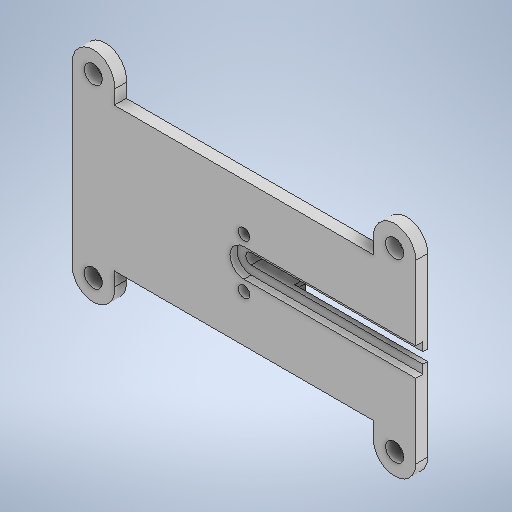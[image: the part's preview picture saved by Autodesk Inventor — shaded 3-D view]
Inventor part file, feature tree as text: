
AUTODESK INVENTOR PART (.ipt)
format: ipt  version: 2025.1 (Build 291241000, 241)  size: 326,656 bytes
history: native  units: mm
features: extrude x4, sketch x4
ambient origin geometry x8: Origin, YZ Plane, XZ Plane, XY Plane, X Axis, Y Axis, Z Axis, Center Point
bodies: Solid1 (feature_tree)
feature tree (8):
  extrude  "Extrusion1"  Depth=15.5mm
  extrude  "Extrusion2"  Depth=2.48mm
  extrude  "Extrusion3"  Depth=10.5mm
  extrude  "Extrusion4"  Depth=20.0mm
  sketch  "Sketch1"  dims[d0=2.48mm d1=15.5mm]
  sketch  "Sketch2"  dims[d2=15.5mm d3=2.48mm]
  sketch  "Sketch3"  dims[d4=10.5mm d5=10.5mm]
  sketch  "Sketch4"  dims[d6=20.0mm d7=20.0mm d8=2.65mm d9=7.25mm d10=2.8mm d11=0.0mm d12=2.5mm d13=33.2mm d14=25.0mm d15=4.9mm d16=4.2mm d17=7.3mm d18=2.75mm d19=0.0mm d20=3.25mm d21=1.65mm d22=0.0mm d25=79.5mm d26=11.75mm d27=14.25mm d28=5.1mm d29=6.6mm d30=8.8mm d31=1.5mm d32=5.1mm d33=6.6mm d34=8.8mm d35=1.5mm d36=2.3mm d37=0.0mm]
